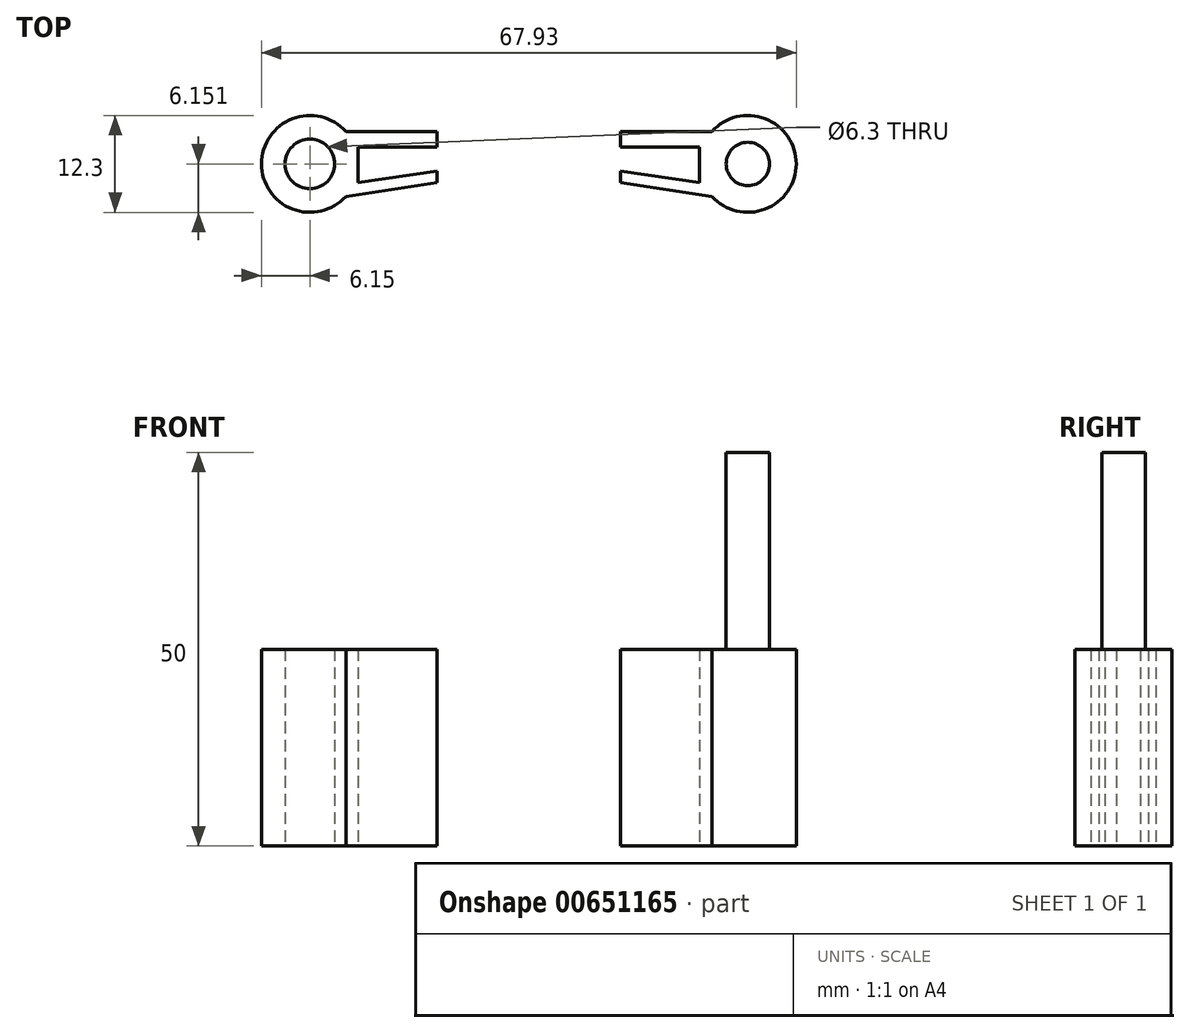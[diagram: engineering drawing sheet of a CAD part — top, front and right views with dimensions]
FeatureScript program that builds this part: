
annotation { "Feature Type Name" : "Feature", "Feature Type Description" : "" }
export const myFeature = defineFeature(function(context is Context, id is Id, definition is map)
    precondition{}
    {
        {
            var Q0;
            Q0=qCreatedBy(makeId("Top.planeOp"),FACE);
            var sketch = newSketch(context, id + "F0", { "sketchPlane" : qUnion([Q0])});
            skLineSegment(sketch, "E0", {"start": v(0, 0) * mm, "end": v(-10, 0) * mm});
            skLineSegment(sketch, "E1", {"start": v(-10, 0) * mm, "end": v(-10, -4.5) * mm});
            skLineSegment(sketch, "E2", {"start": v(-10, -4.5) * mm, "end": v(0, -3) * mm});
            skLineSegment(sketch, "E3", {"start": v(0, 0) * mm, "end": v(0, 2) * mm});
            skLineSegment(sketch, "E4", {"start": v(0, 2) * mm, "end": v(-11.58, 2) * mm});
            skLineSegment(sketch, "E5", {"start": v(-11.58, 2) * mm, "end": v(-11.58, -6.24) * mm, "construction": true});
            skLineSegment(sketch, "E6", {"start": v(-11.58, -6.24) * mm, "end": v(0, -4.5) * mm});
            skLineSegment(sketch, "E7", {"start": v(0, -4.5) * mm, "end": v(0, -3) * mm});
            skCircle(sketch, "E8", {"center": v(-16.15, -2.12) * mm, "radius": 6.15 * mm});
            skCircle(sketch, "E9", {"center": v(-16.15, -2.12) * mm, "radius": 3.15 * mm});
            skLineSegment(sketch, "E10", {"start": v(11.67, 7.07) * mm, "end": v(11.67, -10.4) * mm, "construction": true});
            skLineSegment(sketch, "E11.MirrorCS", {"start": v(23.33, 0) * mm, "end": v(23.33, 2) * mm});
            skLineSegment(sketch, "E12.MirrorCS", {"start": v(23.33, 2) * mm, "end": v(34.92, 2) * mm});
            skCircle(sketch, "E13.MirrorC", {"center": v(39.48, -2.12) * mm, "radius": 6.15 * mm});
            skCircle(sketch, "E14.MirrorC", {"center": v(39.48, -2.12) * mm, "radius": 3.15 * mm, "construction": true});
            skLineSegment(sketch, "E15.MirrorCS", {"start": v(23.33, -4.5) * mm, "end": v(23.33, -3) * mm});
            skLineSegment(sketch, "E16.MirrorCS", {"start": v(33.33, -4.5) * mm, "end": v(23.33, -3) * mm});
            skLineSegment(sketch, "E17.MirrorCS", {"start": v(23.33, 0) * mm, "end": v(33.33, 0) * mm});
            skLineSegment(sketch, "E18.MirrorCS", {"start": v(33.33, 0) * mm, "end": v(33.33, -4.5) * mm});
            skLineSegment(sketch, "E19.MirrorCS", {"start": v(34.92, -6.24) * mm, "end": v(23.33, -4.5) * mm});
            skCircle(sketch, "E20", {"center": v(39.48, -2.12) * mm, "radius": 2.75 * mm});
            skSolve(sketch);
        }
        {
            var Q0;
            {var subQ1=sQuery(id+"F0.wireOp",EDGE,"E0");Q0=makeQuery(id+"F0.imprint","IMPRINT",FACE,{"disambiguationData":[TD([[makeQuery(id+"F0.imprint","IMPRINT",EDGE,{"derivedFrom":subQ1}),-1.0]])]});}
            var Q1;
            Q1=makeQuery(id+"F0.imprint","IMPRINT",FACE,{"disambiguationData":[TD([[makeQuery(id+"F0.imprint","IMPRINT",EDGE,{"derivedFrom":sQuery(id+"F0.wireOp",EDGE,"E9")}),-1.0]])]});
            var Q2;
            {var subQ1=sQuery(id+"F0.wireOp",EDGE,"E2");Q2=makeQuery(id+"F0.imprint","IMPRINT",FACE,{"disambiguationData":[TD([[makeQuery(id+"F0.imprint","IMPRINT",EDGE,{"derivedFrom":subQ1}),-1.0]])]});}
            extrude(context, id + "F1", {"entities" : qUnion([Q0, Q1, Q2]), "depth" : 25 * mm, "offsetDistance" : 25 * mm});
        }
        {
            var Q0;
            Q0=makeQuery(id+"F0.imprint","IMPRINT",FACE,{"disambiguationData":[TD([[makeQuery(id+"F0.imprint","IMPRINT",EDGE,{"derivedFrom":sQuery(id+"F0.wireOp",EDGE,"E20")}),-1.0]])]});
            var Q1;
            Q1=makeQuery(id+"F0.imprint","IMPRINT",FACE,{"disambiguationData":[TD([[makeQuery(id+"F0.imprint","IMPRINT",EDGE,{"derivedFrom":sQuery(id+"F0.wireOp",EDGE,"E11.MirrorCS")}),-1.0]])]});
            var Q2;
            Q2=makeQuery(id+"F0.imprint","IMPRINT",FACE,{"disambiguationData":[TD([[makeQuery(id+"F0.imprint","IMPRINT",EDGE,{"derivedFrom":sQuery(id+"F0.wireOp",EDGE,"E15.MirrorCS")}),-1.0]])]});
            extrude(context, id + "F2", {"entities" : qUnion([Q0, Q1, Q2]), "depth" : 25 * mm, "offsetDistance" : 25 * mm});
        }
        {
            var Q0;
            Q0=makeQuery(id+"F0.imprint","IMPRINT",FACE,{"disambiguationData":[TD([[makeQuery(id+"F0.imprint","IMPRINT",EDGE,{"derivedFrom":sQuery(id+"F0.wireOp",EDGE,"E20")}),1.0]])]});
            extrude(context, id + "F3", {"entities" : qUnion([Q0]), "operationType" : NewBodyOperationType.ADD, "depth" : 50 * mm, "offsetDistance" : 25 * mm});
        }
    });
